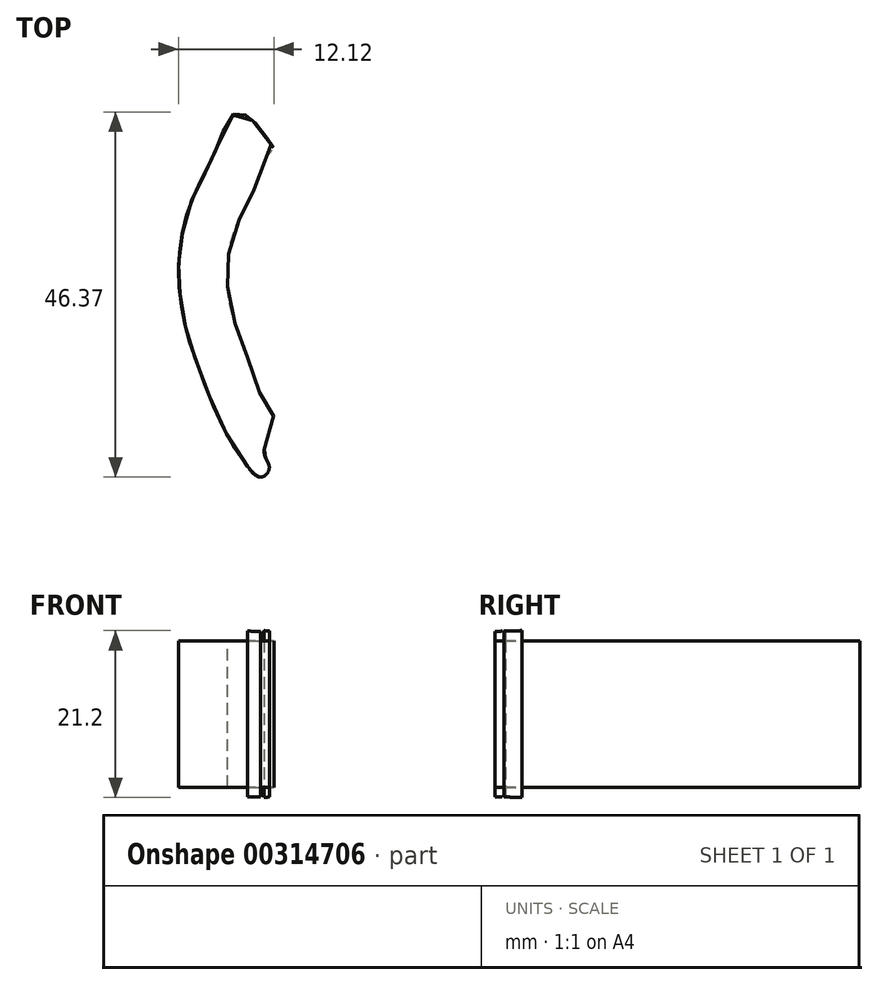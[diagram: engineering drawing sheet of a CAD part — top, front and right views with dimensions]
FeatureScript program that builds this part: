
annotation { "Feature Type Name" : "Feature", "Feature Type Description" : "" }
export const myFeature = defineFeature(function(context is Context, id is Id, definition is map)
    precondition{}
    {
        {
            var Q0;
            Q0=qCreatedBy(makeId("Top.planeOp"),FACE);
            var sketch = newSketch(context, id + "F0", { "sketchPlane" : qUnion([Q0])});
            skFitSpline(sketch, "E0", {"points": [v(-4.7, 0) * mm, v(-6.73, -3.2) * mm, v(-8.07, -6.36) * mm, v(-9.32, -8.76) * mm, v(-10.76, -12.11) * mm, v(-11.72, -15.85) * mm, v(-12.1, -19.21) * mm, v(-12, -22.38) * mm, v(-11.43, -26.21) * mm, v(-10.66, -29.29) * mm, v(-8.93, -34.08) * mm, v(-6.64, -39.64) * mm, v(-3.95, -44.15) * mm, v(-1.55, -46.33) * mm, v(-0.85, -45.88) * mm, v(-0.84, -45.88) * mm, v(-0.57, -45.13) * mm, v(-1.24, -43.1) * mm, v(0, -38.78) * mm, v(-0.97, -37.25) * mm, v(-2.7, -33.12) * mm, v(-4.04, -29.19) * mm, v(-5.67, -24.2) * mm, v(-5.86, -20.07) * mm, v(-5.48, -16.43) * mm, v(-3.66, -12.11) * mm, v(-2.13, -8.95) * mm, v(-0.93, -5.77) * mm, v(0, -4.47) * mm, v(-0.02, -4.47) * mm, v(-1.75, -2.04) * mm, v(-3.09, -0.7) * mm, v(-4.7, 0) * mm]});
            skSolve(sketch);
        }
        {
            var Q0;
            Q0 = qSketchRegion(id + "F0", true);
            extrude(context, id + "F1", {"entities" : qUnion([Q0]), "endBound" : BoundingType.SYMMETRIC, "depth" : 18.62 * mm});
        }
        {
            var Q0;
            Q0=makeQuery(id+"F1.opExtrude","CAP_FACE",FACE,{"disambiguationData":[OSD([sQuery(id+"F0.wireOp",EDGE,"E0")])],"isStart":false});
            var sketch = newSketch(context, id + "F2", { "sketchPlane" : qUnion([Q0])});
            skFitSpline(sketch, "E1", {"points": [v(-3.3, -0.45) * mm, v(-4.32, -1.8) * mm, v(-7.05, -7.1) * mm, v(-10, -14.93) * mm, v(-10.45, -21.87) * mm, v(-8.55, -29.91) * mm, v(-6.06, -36.38) * mm, v(-3.07, -41.1) * mm, v(-1.24, -42.89) * mm, v(-1.04, -43.84) * mm, v(-0.57, -45.15) * mm, v(-1.68, -46.33) * mm, v(-3.66, -44.5) * mm, v(-6.2, -40.4) * mm, v(-7.95, -36.63) * mm, v(-10.94, -28.15) * mm, v(-11.96, -22.8) * mm, v(-11.94, -17.06) * mm, v(-10.78, -12.17) * mm, v(-7.25, -4.47) * mm, v(-5.4, -0.57) * mm, v(-4.24, 0) * mm, v(-3.3, -0.45) * mm]});
            skSolve(sketch);
        }
        {
            var Q0;
            {var subQ0=sQuery(id+"F2.wireOp",EDGE,"E1");var subQ1=makeQuery(id+"F1.opExtrude","CAP_EDGE",EDGE,{"disambiguationData":[OSD([sQuery(id+"F0.wireOp",EDGE,"E0")])],"isStart":false});var subQ11=makeQuery(id+"F2.imprint","INTERSECT",VERTEX,{"disambiguationData":[OD(4.0)],"derivedFrom":[subQ1,subQ0]});var subQ16=makeQuery(id+"F2.imprint","INTERSECT",VERTEX,{"disambiguationData":[OD(5.0)],"derivedFrom":[subQ1,subQ0]});Q0=makeQuery(id+"F2.imprint","IMPRINT",FACE,{"disambiguationData":[TD([[makeQuery(id+"F2.imprint","IMPRINT",EDGE,{"disambiguationData":[TD([[subQ11,1.0],[subQ16,-1.0]])],"derivedFrom":subQ0}),-1.0]])]});}
            extrude(context, id + "F3", {"entities" : qUnion([Q0]), "operationType" : NewBodyOperationType.ADD, "depth" : 2.54 * mm, "hasSecondDirection" : true, "secondDirectionOppositeDirection" : true, "secondDirectionDepth" : 21.16 * mm});
        }
        {
            var Q0;
            Q0=qCreatedBy(makeId("Right.planeOp"),FACE);
            var sketch = newSketch(context, id + "F4", { "sketchPlane" : qUnion([Q0])});
            skLineSegment(sketch, "E2", {"start": v(-46.44, 10.5) * mm, "end": v(2.98, 11.79) * mm});
            skLineSegment(sketch, "E3", {"start": v(2.98, 11.79) * mm, "end": v(2.97, 12.32) * mm});
            skLineSegment(sketch, "E4", {"start": v(2.97, 12.32) * mm, "end": v(-46.44, 12.32) * mm});
            skLineSegment(sketch, "E5", {"start": v(-46.44, 12.32) * mm, "end": v(-46.44, 10.5) * mm});
            skLineSegment(sketch, "E6", {"start": v(-46.44, 12.32) * mm, "end": v(-46.44, 12.32) * mm});
            skLineSegment(sketch, "E7", {"start": v(0, 0) * mm, "end": v(-48.1, 0) * mm, "construction": true});
            skLineSegment(sketch, "E8.MirrorCS", {"start": v(2.97, -12.32) * mm, "end": v(-46.44, -12.32) * mm});
            skLineSegment(sketch, "E9.MirrorCS", {"start": v(-46.44, -10.5) * mm, "end": v(2.98, -11.79) * mm});
            skLineSegment(sketch, "E10.MirrorCS", {"start": v(-46.44, -12.32) * mm, "end": v(-46.44, -10.5) * mm});
            skLineSegment(sketch, "E11.MirrorCS", {"start": v(2.98, -11.79) * mm, "end": v(2.97, -12.32) * mm});
            skSolve(sketch);
        }
        {
            var Q0;
            Q0=makeQuery(id+"F4.imprint","IMPRINT",FACE,{"disambiguationData":[TD([[makeQuery(id+"F4.imprint","IMPRINT",EDGE,{"derivedFrom":sQuery(id+"F4.wireOp",EDGE,"E2")}),1.0]])]});
            var Q1;
            Q1=makeQuery(id+"F4.imprint","IMPRINT",FACE,{"disambiguationData":[TD([[makeQuery(id+"F4.imprint","IMPRINT",EDGE,{"derivedFrom":sQuery(id+"F4.wireOp",EDGE,"E8.MirrorCS")}),-1.0]])]});
            extrude(context, id + "F5", {"entities" : qUnion([Q0, Q1]), "operationType" : NewBodyOperationType.REMOVE, "oppositeDirection" : true, "depth" : 25.4 * mm});
        }
    });
